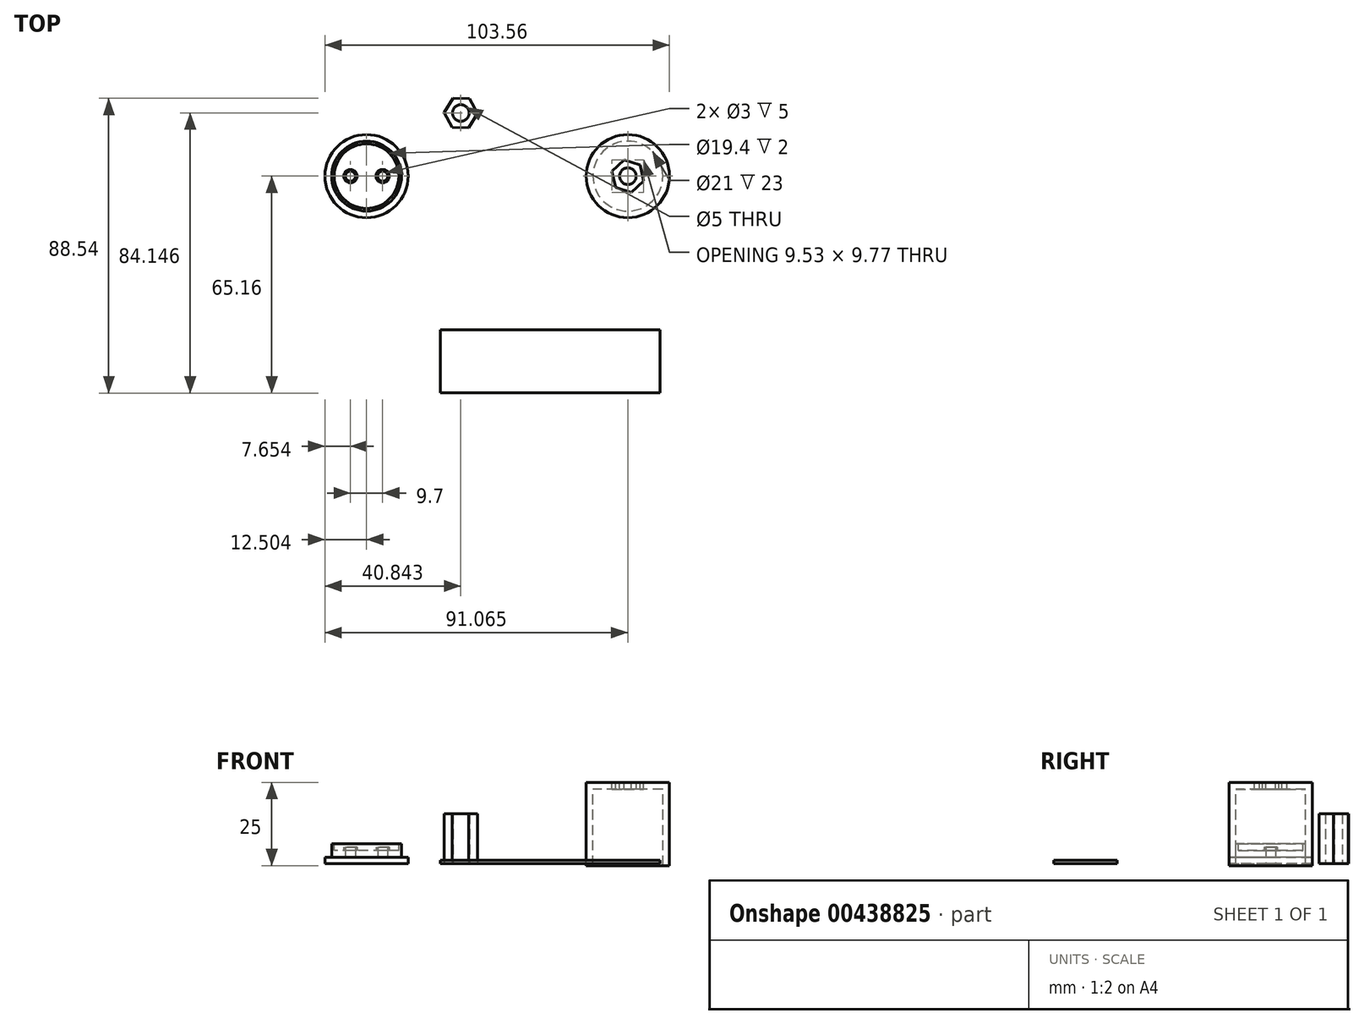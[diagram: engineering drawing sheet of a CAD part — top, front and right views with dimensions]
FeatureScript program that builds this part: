
annotation { "Feature Type Name" : "Feature", "Feature Type Description" : "" }
export const myFeature = defineFeature(function(context is Context, id is Id, definition is map)
    precondition{}
    {
        {
            var Q0;
            Q0=qCreatedBy(makeId("Top.planeOp"),FACE);
            var sketch = newSketch(context, id + "F0", { "sketchPlane" : qUnion([Q0])});
            skCircle(sketch, "E0.cCircle", {"center": v(-30.47, 18.99) * mm, "radius": 4.33 * mm, "construction": true});
            skLineSegment(sketch, "E0.0", {"start": v(-25.47, 18.86) * mm, "end": v(-28.08, 14.6) * mm});
            skLineSegment(sketch, "E0.1", {"start": v(-28.08, 14.6) * mm, "end": v(-33.07, 14.72) * mm});
            skLineSegment(sketch, "E0.2", {"start": v(-33.07, 14.72) * mm, "end": v(-35.47, 19.11) * mm});
            skLineSegment(sketch, "E0.3", {"start": v(-35.47, 19.11) * mm, "end": v(-32.86, 23.38) * mm});
            skLineSegment(sketch, "E0.4", {"start": v(-32.86, 23.38) * mm, "end": v(-27.86, 23.25) * mm});
            skLineSegment(sketch, "E0.5", {"start": v(-27.86, 23.25) * mm, "end": v(-25.47, 18.86) * mm});
            skPoint(sketch, "E0.0.midPoint", {"position": v(-26.77, 16.73) * mm});
            skLineSegment(sketch, "E1", {"start": v(-25.47, 18.86) * mm, "end": v(-35.47, 19.11) * mm});
            skCircle(sketch, "E2", {"center": v(-30.47, 18.99) * mm, "radius": 2.5 * mm});
            skSolve(sketch);
        }
        {
            var Q0;
            {var subQ4=sQuery(id+"F0.wireOp",EDGE,"E0.3");Q0=makeQuery(id+"F0.imprint","IMPRINT",FACE,{"disambiguationData":[TD([[makeQuery(id+"F0.imprint","IMPRINT",EDGE,{"derivedFrom":subQ4}),-1.0]])]});}
            var Q1;
            {var subQ2=sQuery(id+"F0.wireOp",EDGE,"E0.0");Q1=makeQuery(id+"F0.imprint","IMPRINT",FACE,{"disambiguationData":[TD([[makeQuery(id+"F0.imprint","IMPRINT",EDGE,{"derivedFrom":subQ2}),-1.0]])]});}
            extrude(context, id + "F1", {"entities" : qUnion([Q0, Q1]), "depth" : 15 * mm});
        }
        {
            var Q0;
            Q0=qCreatedBy(makeId("Front.planeOp"),FACE);
            var sketch = newSketch(context, id + "F2", { "sketchPlane" : qUnion([Q0])});
            skLineSegment(sketch, "E3", {"start": v(7.25, -0.55) * mm, "end": v(7.25, 24.45) * mm});
            skLineSegment(sketch, "E4", {"start": v(7.25, 24.45) * mm, "end": v(19.75, 24.45) * mm});
            skLineSegment(sketch, "E5", {"start": v(19.75, 24.45) * mm, "end": v(19.75, 22.45) * mm});
            skLineSegment(sketch, "E6", {"start": v(7.25, -0.55) * mm, "end": v(9.25, -0.55) * mm});
            skLineSegment(sketch, "E7", {"start": v(9.25, -0.55) * mm, "end": v(9.25, 22.45) * mm});
            skLineSegment(sketch, "E8", {"start": v(19.75, 22.45) * mm, "end": v(9.25, 22.45) * mm});
            skSolve(sketch);
        }
        {
            var Q0;
            Q0=makeQuery(id+"F2.imprint","IMPRINT",FACE,{"disambiguationData":[TD([[makeQuery(id+"F2.imprint","IMPRINT",EDGE,{"derivedFrom":sQuery(id+"F2.wireOp",EDGE,"E3")}),-1.0]])]});
            var Q1;
            Q1=sQuery(id+"F2.wireOp",EDGE,"E5");
            revolve(context, id + "F3", {"entities" : qUnion([Q0]), "axis" : qUnion([Q1]), "revolveType" : RevolveType.FULL});
        }
        {
            var Q0;
            Q0=makeQuery(id+"F3.opRevolve","SWEPT_FACE",FACE,{"disambiguationData":[OSD([sQuery(id+"F2.wireOp",EDGE,"E4")])]});
            var sketch = newSketch(context, id + "F4", { "sketchPlane" : qUnion([Q0])});
            skCircle(sketch, "E9.cCircle", {"center": v(19.75, 0) * mm, "radius": 4.33 * mm, "construction": true});
            skLineSegment(sketch, "E9.0", {"start": v(18.68, 4.88) * mm, "end": v(23.45, 3.37) * mm});
            skLineSegment(sketch, "E9.1", {"start": v(23.45, 3.37) * mm, "end": v(24.52, -1.51) * mm});
            skLineSegment(sketch, "E9.2", {"start": v(24.52, -1.51) * mm, "end": v(20.83, -4.88) * mm});
            skLineSegment(sketch, "E9.3", {"start": v(20.83, -4.88) * mm, "end": v(16.06, -3.37) * mm});
            skLineSegment(sketch, "E9.4", {"start": v(16.06, -3.37) * mm, "end": v(14.99, 1.51) * mm});
            skLineSegment(sketch, "E9.5", {"start": v(14.99, 1.51) * mm, "end": v(18.68, 4.88) * mm});
            skPoint(sketch, "E9.0.midPoint", {"position": v(21.07, 4.13) * mm});
            skLineSegment(sketch, "E10", {"start": v(14.99, 1.51) * mm, "end": v(24.52, -1.51) * mm});
            skCircle(sketch, "E11", {"center": v(19.75, 0) * mm, "radius": 2.5 * mm});
            skSolve(sketch);
        }
        {
            var Q0;
            {var subQ0=sQuery(id+"F4.wireOp",EDGE,"E11");var subQ1=sQuery(id+"F4.wireOp",EDGE,"E10");var subQ2=makeQuery(id+"F4.imprint","INTERSECT",VERTEX,{"disambiguationData":[OD(0.0)],"derivedFrom":[subQ1,subQ0]});Q0=makeQuery(id+"F4.imprint","IMPRINT",FACE,{"disambiguationData":[TD([[makeQuery(id+"F4.imprint","IMPRINT",EDGE,{"disambiguationData":[TD([[subQ2,-1.0]])],"derivedFrom":subQ1}),-1.0]])]});}
            var Q1;
            {var subQ0=sQuery(id+"F4.wireOp",EDGE,"E11");var subQ1=sQuery(id+"F4.wireOp",EDGE,"E10");var subQ2=makeQuery(id+"F4.imprint","INTERSECT",VERTEX,{"disambiguationData":[OD(0.0)],"derivedFrom":[subQ1,subQ0]});Q1=makeQuery(id+"F4.imprint","IMPRINT",FACE,{"disambiguationData":[TD([[makeQuery(id+"F4.imprint","IMPRINT",EDGE,{"disambiguationData":[TD([[subQ2,-1.0]])],"derivedFrom":subQ1}),1.0]])]});}
            extrude(context, id + "F5", {"entities" : qUnion([Q0, Q1]), "operationType" : NewBodyOperationType.REMOVE, "oppositeDirection" : true, "depth" : 25 * mm});
        }
        {
            var Q0;
            Q0=makeQuery(id+"F4.imprint","IMPRINT",FACE,{"disambiguationData":[TD([[makeQuery(id+"F4.imprint","IMPRINT",EDGE,{"derivedFrom":sQuery(id+"F4.wireOp",EDGE,"E9.0")}),-1.0]])]});
            var Q1;
            {var subQ4=sQuery(id+"F4.wireOp",EDGE,"E9.2");Q1=makeQuery(id+"F4.imprint","IMPRINT",FACE,{"disambiguationData":[TD([[makeQuery(id+"F4.imprint","IMPRINT",EDGE,{"derivedFrom":subQ4}),-1.0]])]});}
            extrude(context, id + "F6", {"entities" : qUnion([Q0, Q1]), "operationType" : NewBodyOperationType.REMOVE, "oppositeDirection" : true, "depth" : 1.25 * mm});
        }
        {
            var Q0;
            Q0=qCreatedBy(makeId("Front.planeOp"),FACE);
            var sketch = newSketch(context, id + "F7", { "sketchPlane" : qUnion([Q0])});
            skLineSegment(sketch, "E12", {"start": v(-71.3, 0) * mm, "end": v(-46.3, 0) * mm});
            skLineSegment(sketch, "E13", {"start": v(-71.3, 0) * mm, "end": v(-71.3, 2) * mm});
            skLineSegment(sketch, "E14", {"start": v(-46.3, 0) * mm, "end": v(-46.3, 2) * mm});
            skLineSegment(sketch, "E15", {"start": v(-71.3, 2) * mm, "end": v(-69.3, 2) * mm});
            skLineSegment(sketch, "E16", {"start": v(-46.3, 2) * mm, "end": v(-48.3, 2) * mm});
            skLineSegment(sketch, "E17", {"start": v(-69.3, 2) * mm, "end": v(-69.3, 4) * mm});
            skLineSegment(sketch, "E18", {"start": v(-48.3, 2) * mm, "end": v(-48.3, 4) * mm});
            skLineSegment(sketch, "E19", {"start": v(-48.3, 4) * mm, "end": v(-69.3, 4) * mm});
            skLineSegment(sketch, "E20", {"start": v(-58.8, 4) * mm, "end": v(-58.8, 0) * mm});
            skLineSegment(sketch, "E21", {"start": v(-69.3, 4) * mm, "end": v(-69.3, 6) * mm});
            skLineSegment(sketch, "E22", {"start": v(-69.3, 6) * mm, "end": v(-68.5, 6) * mm});
            skLineSegment(sketch, "E23", {"start": v(-68.5, 6) * mm, "end": v(-68.5, 4) * mm});
            skLineSegment(sketch, "E24", {"start": v(-48.3, 4) * mm, "end": v(-48.3, 6) * mm});
            skLineSegment(sketch, "E25", {"start": v(-48.3, 6) * mm, "end": v(-49.1, 6) * mm});
            skLineSegment(sketch, "E26", {"start": v(-49.1, 6) * mm, "end": v(-49.1, 4) * mm});
            skSolve(sketch);
        }
        {
            var Q0;
            {var subQ1=sQuery(id+"F7.wireOp",EDGE,"E13");Q0=makeQuery(id+"F7.imprint","IMPRINT",FACE,{"disambiguationData":[TD([[makeQuery(id+"F7.imprint","IMPRINT",EDGE,{"derivedFrom":subQ1}),-1.0]])]});}
            var Q1;
            {var subQ0=sQuery(id+"F7.wireOp",EDGE,"E21");Q1=makeQuery(id+"F7.imprint","IMPRINT",FACE,{"disambiguationData":[TD([[makeQuery(id+"F7.imprint","IMPRINT",EDGE,{"derivedFrom":subQ0}),-1.0]])]});}
            var Q2;
            Q2=sQuery(id+"F7.wireOp",EDGE,"E20");
            revolve(context, id + "F8", {"entities" : qUnion([Q0, Q1]), "axis" : qUnion([Q2]), "revolveType" : RevolveType.FULL});
        }
        {
            var Q0;
            Q0=makeQuery(id+"F8.opRevolve","SWEPT_FACE",FACE,{"disambiguationData":[OSD([sQuery(id+"F7.wireOp",EDGE,"E19")])]});
            var sketch = newSketch(context, id + "F9", { "sketchPlane" : qUnion([Q0])});
            skLineSegment(sketch, "E27", {"start": v(-58.8, 0) * mm, "end": v(-63.66, 0) * mm});
            skLineSegment(sketch, "E28", {"start": v(-58.8, 0) * mm, "end": v(-53.96, 0) * mm});
            skCircle(sketch, "E29", {"center": v(-63.66, 0) * mm, "radius": 2 * mm});
            skCircle(sketch, "E30", {"center": v(-53.96, 0) * mm, "radius": 2 * mm});
            skCircle(sketch, "E31", {"center": v(-63.66, 0) * mm, "radius": 1.5 * mm});
            skCircle(sketch, "E32", {"center": v(-53.96, 0) * mm, "radius": 1.5 * mm});
            skSolve(sketch);
        }
        {
            var Q0;
            Q0=makeQuery(id+"F9.imprint","IMPRINT",FACE,{"disambiguationData":[TD([[makeQuery(id+"F9.imprint","IMPRINT",EDGE,{"derivedFrom":sQuery(id+"F9.wireOp",EDGE,"E29")}),1.0]])]});
            var Q1;
            Q1=makeQuery(id+"F9.imprint","IMPRINT",FACE,{"disambiguationData":[TD([[makeQuery(id+"F9.imprint","IMPRINT",EDGE,{"derivedFrom":sQuery(id+"F9.wireOp",EDGE,"E30")}),1.0]])]});
            extrude(context, id + "F10", {"entities" : qUnion([Q0, Q1]), "operationType" : NewBodyOperationType.ADD, "depth" : 1 * mm});
        }
        {
            var Q0;
            Q0=makeQuery(id+"F10.boolean.opBoolean","SPLIT",FACE,{"disambiguationData":[TD([makeQuery(id+"F10.opExtrude","SWEPT_FACE",FACE,{"disambiguationData":[OSD([sQuery(id+"F9.wireOp",EDGE,"E32")])]})])],"derivedFrom":makeQuery(id+"F8.opRevolve","SWEPT_FACE",FACE,{"disambiguationData":[OSD([sQuery(id+"F7.wireOp",EDGE,"E19")])]})});
            var Q1;
            Q1=makeQuery(id+"F10.boolean.opBoolean","SPLIT",FACE,{"disambiguationData":[TD([makeQuery(id+"F10.opExtrude","SWEPT_FACE",FACE,{"disambiguationData":[OSD([sQuery(id+"F9.wireOp",EDGE,"E31")])]})])],"derivedFrom":makeQuery(id+"F8.opRevolve","SWEPT_FACE",FACE,{"disambiguationData":[OSD([sQuery(id+"F7.wireOp",EDGE,"E19")])]})});
            extrude(context, id + "F11", {"entities" : qUnion([Q0, Q1]), "operationType" : NewBodyOperationType.REMOVE, "oppositeDirection" : true, "depth" : 25 * mm});
        }
        {
            var Q0;
            Q0=qCreatedBy(makeId("Top.planeOp"),FACE);
            var sketch = newSketch(context, id + "F12", { "sketchPlane" : qUnion([Q0])});
            skLineSegment(sketch, "E33", {"start": v(-36.6, -46.16) * mm, "end": v(29.4, -46.16) * mm});
            skLineSegment(sketch, "E34", {"start": v(29.4, -46.16) * mm, "end": v(29.4, -65.16) * mm});
            skLineSegment(sketch, "E35", {"start": v(29.4, -65.16) * mm, "end": v(-36.6, -65.16) * mm});
            skLineSegment(sketch, "E36", {"start": v(-36.6, -65.16) * mm, "end": v(-36.6, -46.16) * mm});
            skLineSegment(sketch, "E37", {"start": v(-36.6, -65.16) * mm, "end": v(-36.6, -66.66) * mm});
            skLineSegment(sketch, "E38", {"start": v(-36.6, -65.16) * mm, "end": v(-38.1, -65.16) * mm});
            skLineSegment(sketch, "E39", {"start": v(29.4, -65.16) * mm, "end": v(29.4, -66.66) * mm});
            skLineSegment(sketch, "E40", {"start": v(29.4, -65.16) * mm, "end": v(30.9, -65.16) * mm});
            skLineSegment(sketch, "E41", {"start": v(29.4, -46.16) * mm, "end": v(29.4, -44.66) * mm});
            skLineSegment(sketch, "E42", {"start": v(29.4, -46.16) * mm, "end": v(30.9, -46.16) * mm});
            skLineSegment(sketch, "E43", {"start": v(-36.6, -46.16) * mm, "end": v(-36.6, -44.66) * mm});
            skLineSegment(sketch, "E44", {"start": v(-36.6, -46.16) * mm, "end": v(-38.1, -46.16) * mm});
            skLineSegment(sketch, "E45", {"start": v(-38.1, -46.16) * mm, "end": v(-38.1, -44.67) * mm});
            skLineSegment(sketch, "E46", {"start": v(-38.1, -44.67) * mm, "end": v(-36.6, -44.66) * mm});
            skLineSegment(sketch, "E47", {"start": v(-38.1, -65.16) * mm, "end": v(-38.1, -66.66) * mm});
            skLineSegment(sketch, "E48", {"start": v(-38.1, -66.66) * mm, "end": v(-36.6, -66.66) * mm});
            skLineSegment(sketch, "E49", {"start": v(29.4, -66.66) * mm, "end": v(30.91, -66.66) * mm});
            skLineSegment(sketch, "E50", {"start": v(30.91, -66.66) * mm, "end": v(30.9, -65.16) * mm});
            skLineSegment(sketch, "E51", {"start": v(29.4, -44.66) * mm, "end": v(30.9, -44.66) * mm});
            skLineSegment(sketch, "E52", {"start": v(30.9, -44.66) * mm, "end": v(30.9, -46.16) * mm});
            skLineSegment(sketch, "E53", {"start": v(30.9, -46.16) * mm, "end": v(30.9, -65.16) * mm});
            skLineSegment(sketch, "E54", {"start": v(29.4, -66.66) * mm, "end": v(-36.6, -66.66) * mm});
            skLineSegment(sketch, "E55", {"start": v(-38.1, -65.16) * mm, "end": v(-38.1, -46.16) * mm});
            skLineSegment(sketch, "E56", {"start": v(-36.6, -44.66) * mm, "end": v(29.4, -44.66) * mm});
            skSolve(sketch);
        }
        {
            var Q0;
            Q0=makeQuery(id+"F12.imprint","IMPRINT",FACE,{"disambiguationData":[TD([[makeQuery(id+"F12.imprint","IMPRINT",EDGE,{"derivedFrom":sQuery(id+"F12.wireOp",EDGE,"E33")}),-1.0]])]});
            extrude(context, id + "F13", {"entities" : qUnion([Q0]), "depth" : 1 * mm});
        }
    });
